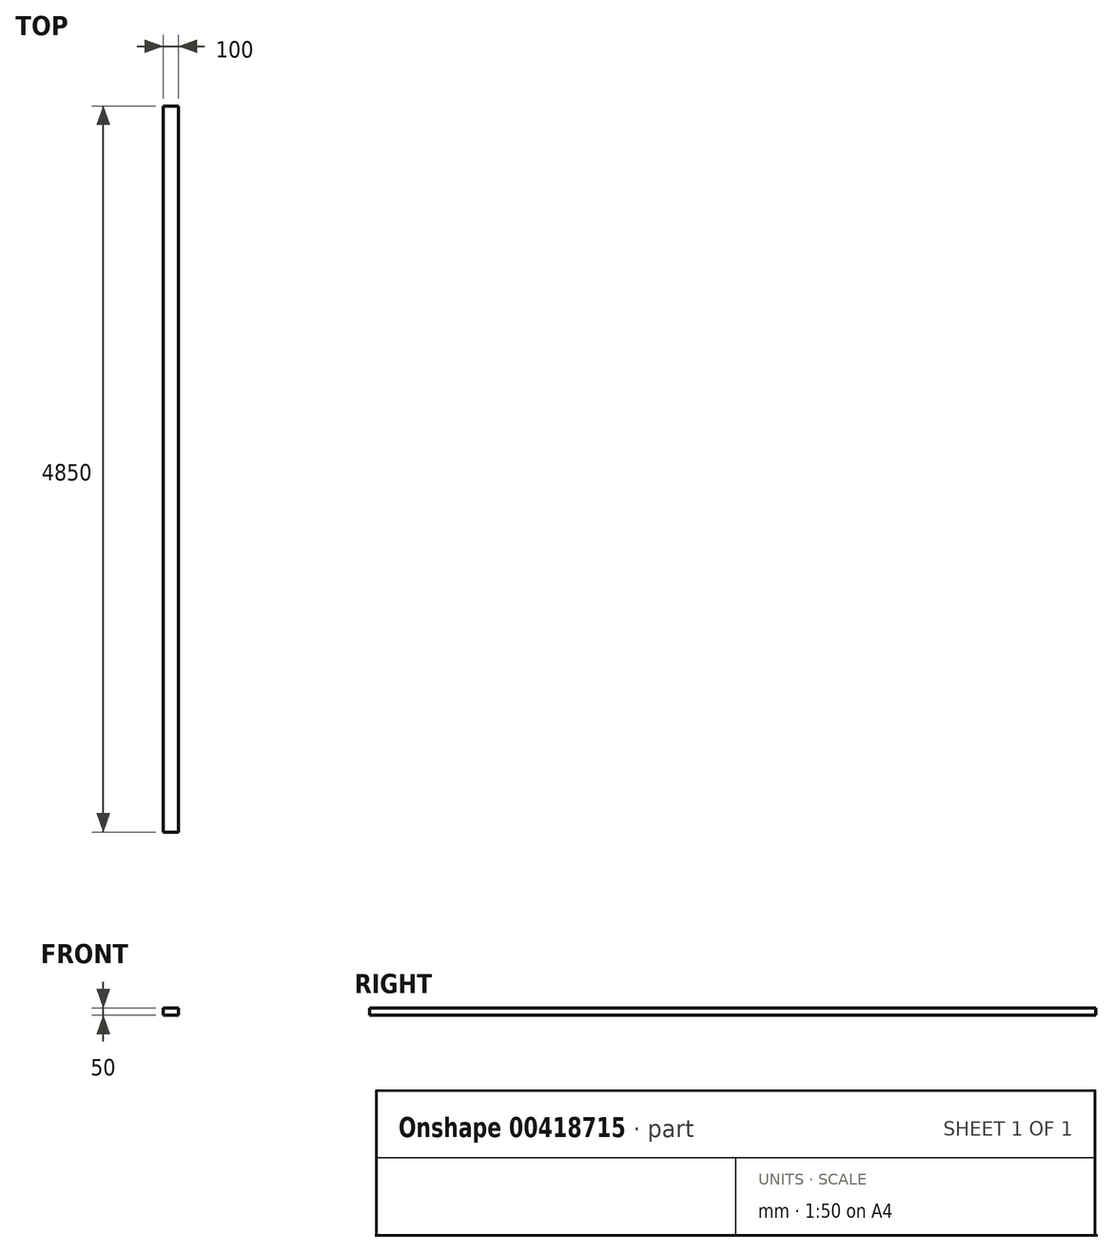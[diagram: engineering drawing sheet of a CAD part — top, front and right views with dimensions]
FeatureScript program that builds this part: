
annotation { "Feature Type Name" : "Feature", "Feature Type Description" : "" }
export const myFeature = defineFeature(function(context is Context, id is Id, definition is map)
    precondition{}
    {
        {
            var Q0;
            Q0=qCreatedBy(makeId("Front.planeOp"),FACE);
            var sketch = newSketch(context, id + "F0", { "sketchPlane" : qUnion([Q0])});
            skLineSegment(sketch, "E0.bottom", {"start": v(50, 25) * mm, "end": v(-50, 25) * mm});
            skLineSegment(sketch, "E0.top", {"start": v(50, -25) * mm, "end": v(-50, -25) * mm});
            skLineSegment(sketch, "E0.left", {"start": v(50, 25) * mm, "end": v(50, -25) * mm});
            skLineSegment(sketch, "E0.right", {"start": v(-50, 25) * mm, "end": v(-50, -25) * mm});
            skPoint(sketch, "E0.middle", {"position": v(0, 0) * mm});
            skSolve(sketch);
        }
        {
            var Q0;
            Q0 = qSketchRegion(id + "F0", true);
            extrude(context, id + "F1", {"entities" : qUnion([Q0]), "endBound" : BoundingType.SYMMETRIC, "depth" : 4850 * mm});
        }
    });
